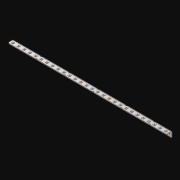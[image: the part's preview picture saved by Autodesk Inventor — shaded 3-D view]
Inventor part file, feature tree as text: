
AUTODESK INVENTOR PART (.ipt)
format: ipt  version: 2021 (Build 250183000, 183)  size: 803,328 bytes
history: native  units: in
note: dims shown in document units (in); Inventor stores cm internally (conversion verified against a paired STEP export)
features: extrude x57, other x56, sketch x3, pattern_linear x1, sheet_metal_op x1
ambient origin geometry x8: Origin, YZ Plane, XZ Plane, XY Plane, X Axis, Y Axis, Z Axis, Center Point
bodies: Solid1 (feature_tree)
feature tree (118):
  pattern_linear  "Rectangular Pattern1"  Spacing1=0.063in  [1 undecoded]
  extrude  "Extrusion1"  Depth=0.5in
  sketch  "Sketch1"  dims[d0=0.182in]
  other  "Srf1"
  sketch  "Sketch2"  dims[d1=0.063in d2=0.0in]
  other  "Srf2"
  other  "Srf3"
  other  "Srf5"
  other  "Srf7"
  other  "Srf9"
  other  "Srf11"
  other  "Srf13"
  other  "Srf15"
  other  "Srf17"
  other  "Srf19"
  other  "Srf21"
  other  "Srf23"
  other  "Srf25"
  other  "Srf27"
  other  "Srf29"
  other  "Srf31"
  other  "Srf33"
  other  "Srf35"
  other  "Srf37"
  other  "Srf39"
  other  "Srf41"
  other  "Srf43"
  other  "Srf45"
  other  "Srf47"
  other  "Srf49"
  other  "Srf51"
  other  "Srf53"
  other  "Srf55"
  other  "Srf4"
  other  "Srf6"
  other  "Srf8"
  other  "Srf10"
  other  "Srf12"
  other  "Srf14"
  other  "Srf16"
  other  "Srf18"
  other  "Srf20"
  other  "Srf22"
  other  "Srf24"
  other  "Srf26"
  other  "Srf28"
  other  "Srf30"
  other  "Srf32"
  other  "Srf34"
  other  "Srf36"
  other  "Srf38"
  other  "Srf40"
  other  "Srf42"
  other  "Srf44"
  other  "Srf46"
  other  "Srf48"
  other  "Srf50"
  other  "Srf52"
  other  "Srf54"
  other  "Srf56"
  sketch  "Sketch3"  dims[d3=0.182in d4=0.063in d5=0.0in d8=0.5in d9=3.5in d10=0.0in]
  sheet_metal_op  "Fold1"
  extrude  "ExtrusionSrf1"  Depth=0.5in TaperAngle=0.0deg
  extrude  "ExtrusionSrf2"  [1 undecoded]
  extrude  "ExtrusionSrf3"  [1 undecoded]
  extrude  "ExtrusionSrf4"  [1 undecoded]
  extrude  "ExtrusionSrf5"  [1 undecoded]
  extrude  "ExtrusionSrf6"  [1 undecoded]
  extrude  "ExtrusionSrf7"  [1 undecoded]
  extrude  "ExtrusionSrf8"  [1 undecoded]
  extrude  "ExtrusionSrf9"  [1 undecoded]
  extrude  "ExtrusionSrf10"  [1 undecoded]
  extrude  "ExtrusionSrf11"  [1 undecoded]
  extrude  "ExtrusionSrf12"  [1 undecoded]
  extrude  "ExtrusionSrf13"  [1 undecoded]
  extrude  "ExtrusionSrf14"  [1 undecoded]
  extrude  "ExtrusionSrf15"  [1 undecoded]
  extrude  "ExtrusionSrf16"  [1 undecoded]
  extrude  "ExtrusionSrf17"  [1 undecoded]
  extrude  "ExtrusionSrf18"  [1 undecoded]
  extrude  "ExtrusionSrf19"  [1 undecoded]
  extrude  "ExtrusionSrf20"  [1 undecoded]
  extrude  "ExtrusionSrf21"  [1 undecoded]
  extrude  "ExtrusionSrf22"  [1 undecoded]
  extrude  "ExtrusionSrf23"  [1 undecoded]
  extrude  "ExtrusionSrf24"  [1 undecoded]
  extrude  "ExtrusionSrf25"  [1 undecoded]
  extrude  "ExtrusionSrf26"  [1 undecoded]
  extrude  "ExtrusionSrf27"  [1 undecoded]
  extrude  "ExtrusionSrf28"  [1 undecoded]
  extrude  "ExtrusionSrf29"  [1 undecoded]
  extrude  "ExtrusionSrf37"  [1 undecoded]
  extrude  "ExtrusionSrf38"  [1 undecoded]
  extrude  "ExtrusionSrf39"  [1 undecoded]
  extrude  "ExtrusionSrf40"  [1 undecoded]
  extrude  "ExtrusionSrf41"  [1 undecoded]
  extrude  "ExtrusionSrf42"  [1 undecoded]
  extrude  "ExtrusionSrf43"  [1 undecoded]
  extrude  "ExtrusionSrf44"  [1 undecoded]
  extrude  "ExtrusionSrf45"  [1 undecoded]
  extrude  "ExtrusionSrf46"  [1 undecoded]
  extrude  "ExtrusionSrf47"  [1 undecoded]
  extrude  "ExtrusionSrf48"  [1 undecoded]
  extrude  "ExtrusionSrf49"  [1 undecoded]
  extrude  "ExtrusionSrf50"  [1 undecoded]
  extrude  "ExtrusionSrf51"  [1 undecoded]
  extrude  "ExtrusionSrf52"  [1 undecoded]
  extrude  "ExtrusionSrf53"  [1 undecoded]
  extrude  "ExtrusionSrf54"  [1 undecoded]
  extrude  "ExtrusionSrf55"  [1 undecoded]
  extrude  "ExtrusionSrf56"  [1 undecoded]
  extrude  "ExtrusionSrf57"  [1 undecoded]
  extrude  "ExtrusionSrf58"  [1 undecoded]
  extrude  "ExtrusionSrf59"  [1 undecoded]
  extrude  "ExtrusionSrf60"  [1 undecoded]
  extrude  "ExtrusionSrf61"  [1 undecoded]
  extrude  "ExtrusionSrf62"  [1 undecoded]
  extrude  "ExtrusionSrf63"  [1 undecoded]
note: 56 required parameter values undecoded (feature->parameter linkage not recoverable at this tier; creation-order binding heuristic only, values carry confidence <= 0.55)
